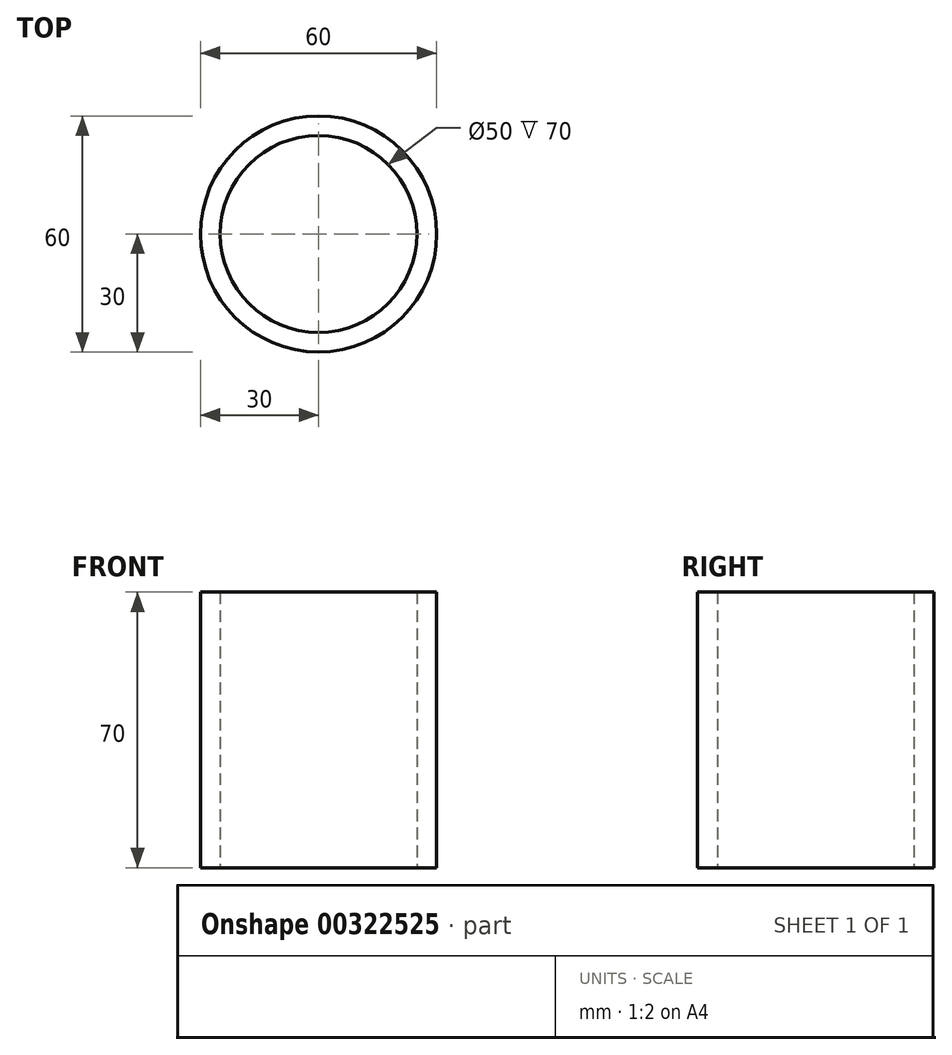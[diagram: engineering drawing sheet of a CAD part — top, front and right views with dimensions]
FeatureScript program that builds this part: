
annotation { "Feature Type Name" : "Feature", "Feature Type Description" : "" }
export const myFeature = defineFeature(function(context is Context, id is Id, definition is map)
    precondition{}
    {
        {
            var Q0;
            Q0=qCreatedBy(makeId("Top.planeOp"),FACE);
            var sketch = newSketch(context, id + "F0", { "sketchPlane" : qUnion([Q0])});
            skCircle(sketch, "E0", {"center": v(0, 0) * mm, "radius": 30 * mm});
            skCircle(sketch, "E1", {"center": v(0, 0) * mm, "radius": 25 * mm});
            skSolve(sketch);
        }
        {
            var Q0;
            Q0 = qSketchRegion(id + "F0", true);
            extrude(context, id + "F1", {"entities" : qUnion([Q0]), "depth" : 70 * mm});
        }
    });
